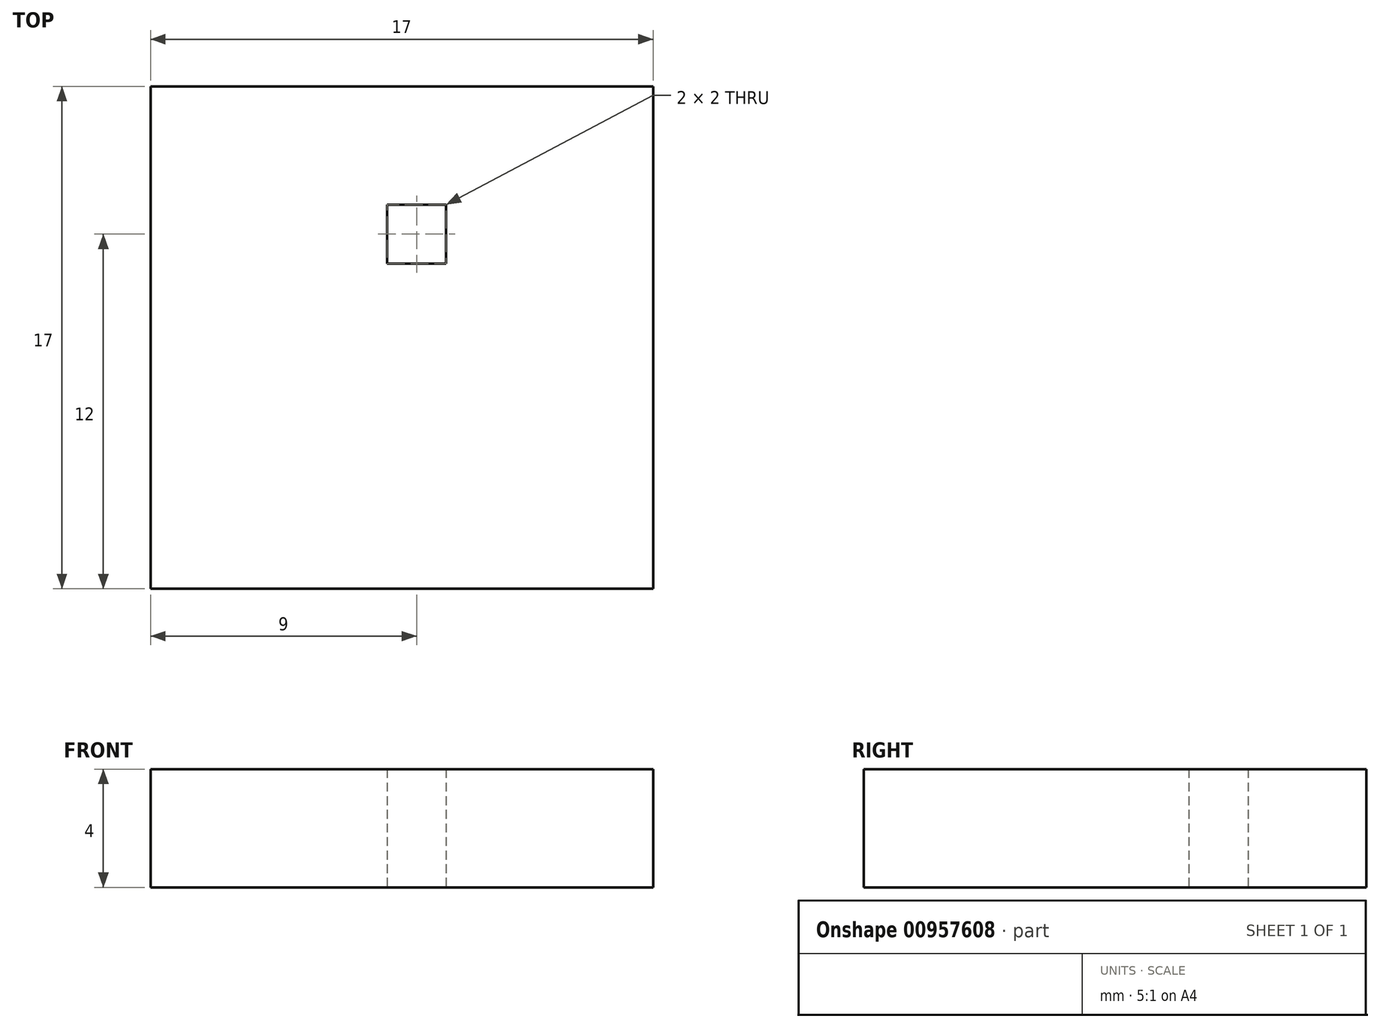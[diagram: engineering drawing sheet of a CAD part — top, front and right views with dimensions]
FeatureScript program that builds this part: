
annotation { "Feature Type Name" : "Feature", "Feature Type Description" : "" }
export const myFeature = defineFeature(function(context is Context, id is Id, definition is map)
    precondition{}
    {
        {
            var Q0;
            Q0=qCreatedBy(makeId("Top.planeOp"),FACE);
            var sketch = newSketch(context, id + "F0", { "sketchPlane" : qUnion([Q0])});
            skLineSegment(sketch, "E0.bottom", {"start": v(-8.5, 8.5) * mm, "end": v(8.5, 8.5) * mm});
            skLineSegment(sketch, "E0.top", {"start": v(-8.5, -8.5) * mm, "end": v(8.5, -8.5) * mm});
            skLineSegment(sketch, "E0.left", {"start": v(-8.5, 8.5) * mm, "end": v(-8.5, -8.5) * mm});
            skLineSegment(sketch, "E0.right", {"start": v(8.5, 8.5) * mm, "end": v(8.5, -8.5) * mm});
            skPoint(sketch, "E0.middle", {"position": v(0, 0) * mm});
            skLineSegment(sketch, "E1.bottom", {"start": v(1.5, 4.5) * mm, "end": v(-0.5, 4.5) * mm});
            skLineSegment(sketch, "E1.top", {"start": v(1.5, 2.5) * mm, "end": v(-0.5, 2.5) * mm});
            skLineSegment(sketch, "E1.left", {"start": v(1.5, 4.5) * mm, "end": v(1.5, 2.5) * mm});
            skLineSegment(sketch, "E1.right", {"start": v(-0.5, 4.5) * mm, "end": v(-0.5, 2.5) * mm});
            skSolve(sketch);
        }
        {
            var Q0;
            Q0=makeQuery(id+"F0.imprint","IMPRINT",FACE,{"disambiguationData":[TD([[makeQuery(id+"F0.imprint","IMPRINT",EDGE,{"derivedFrom":sQuery(id+"F0.wireOp",EDGE,"E0.bottom")}),-1.0]])]});
            extrude(context, id + "F1", {"entities" : qUnion([Q0]), "depth" : 4 * mm, "offsetDistance" : 25 * mm});
        }
    });
